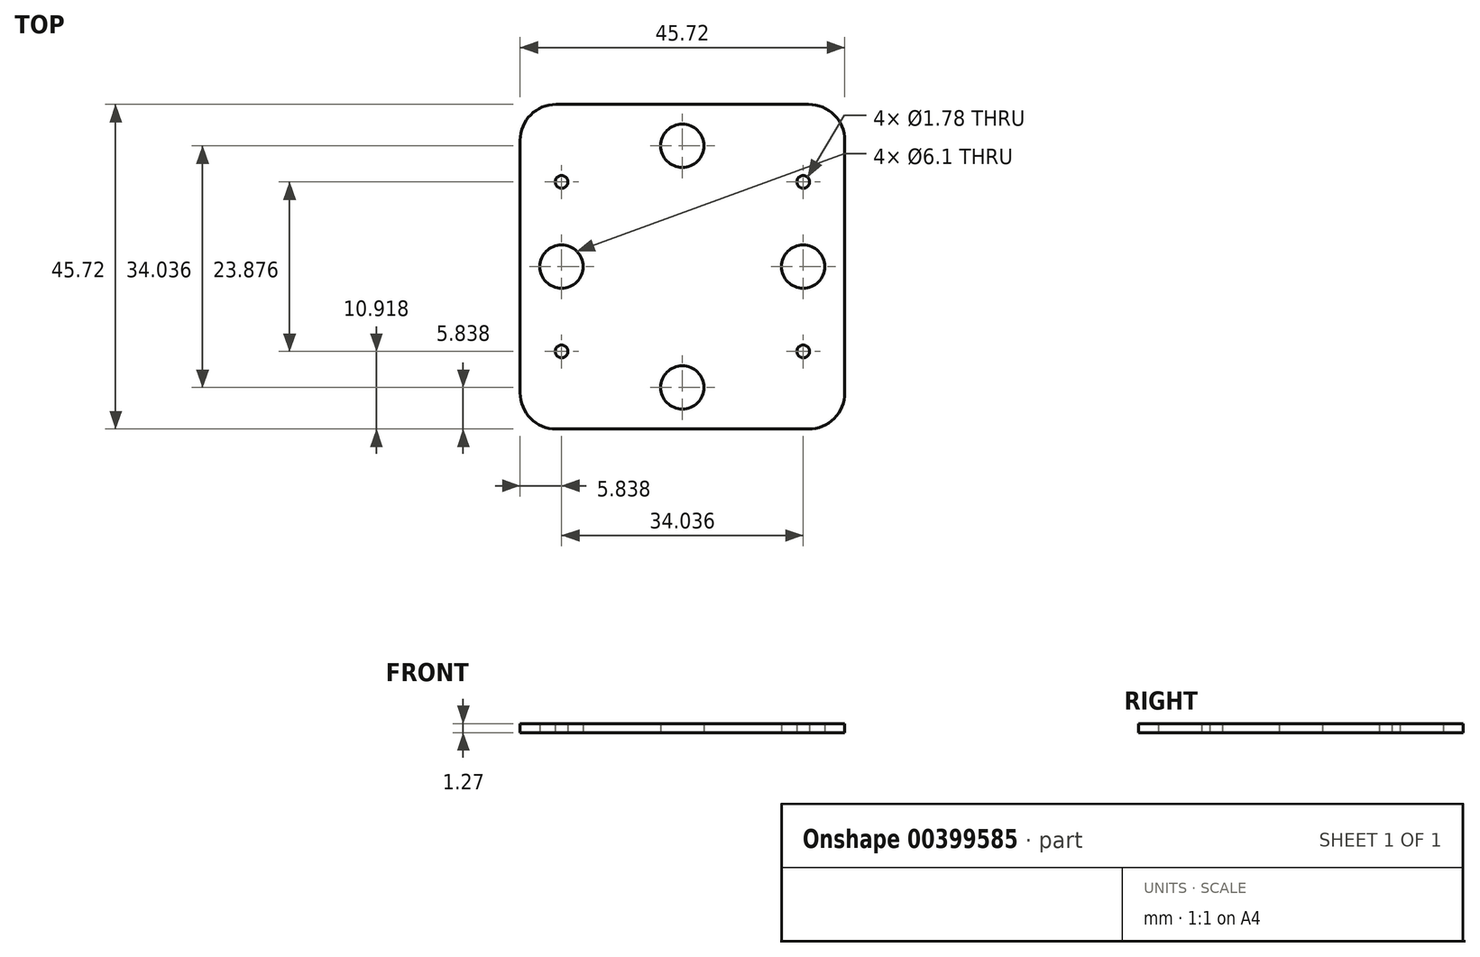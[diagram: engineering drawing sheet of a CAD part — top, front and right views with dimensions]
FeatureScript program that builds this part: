
annotation { "Feature Type Name" : "Feature", "Feature Type Description" : "" }
export const myFeature = defineFeature(function(context is Context, id is Id, definition is map)
    precondition{}
    {
        {
            var Q0;
            Q0=qCreatedBy(makeId("Top.planeOp"),FACE);
            var sketch = newSketch(context, id + "F0", { "sketchPlane" : qUnion([Q0])});
            skLineSegment(sketch, "E0.bottom", {"start": v(-5.96, 25.9) * mm, "end": v(39.76, 25.9) * mm});
            skLineSegment(sketch, "E0.top", {"start": v(-5.96, -19.81) * mm, "end": v(39.76, -19.81) * mm});
            skLineSegment(sketch, "E0.left", {"start": v(-5.96, 25.9) * mm, "end": v(-5.96, -19.81) * mm});
            skLineSegment(sketch, "E0.right", {"start": v(39.76, 25.9) * mm, "end": v(39.76, -19.81) * mm});
            skLineSegment(sketch, "E1.bottom", {"start": v(-0.12, 20.06) * mm, "end": v(33.91, 20.06) * mm});
            skLineSegment(sketch, "E1.top", {"start": v(-0.12, -13.97) * mm, "end": v(33.91, -13.97) * mm});
            skLineSegment(sketch, "E1.left", {"start": v(-0.12, 20.06) * mm, "end": v(-0.12, -13.97) * mm});
            skLineSegment(sketch, "E1.right", {"start": v(33.91, 20.06) * mm, "end": v(33.91, -13.97) * mm});
            skCircle(sketch, "E2", {"center": v(-0.12, 3.05) * mm, "radius": 3.05 * mm});
            skCircle(sketch, "E3", {"center": v(16.9, -13.97) * mm, "radius": 3.05 * mm});
            skCircle(sketch, "E4", {"center": v(33.91, 3.05) * mm, "radius": 3.05 * mm});
            skCircle(sketch, "E5", {"center": v(16.9, 20.06) * mm, "radius": 3.05 * mm});
            skCircle(sketch, "E6", {"center": v(-0.12, 14.98) * mm, "radius": 0.89 * mm});
            skCircle(sketch, "E7", {"center": v(-0.12, -8.9) * mm, "radius": 0.89 * mm});
            skCircle(sketch, "E8", {"center": v(33.91, 14.98) * mm, "radius": 0.89 * mm});
            skCircle(sketch, "E9", {"center": v(33.91, -8.9) * mm, "radius": 0.89 * mm});
            skSolve(sketch);
        }
        {
            var Q0;
            Q0=makeQuery(id+"F0.imprint","IMPRINT",FACE,{"disambiguationData":[TD([[makeQuery(id+"F0.imprint","IMPRINT",EDGE,{"derivedFrom":sQuery(id+"F0.wireOp",EDGE,"E0.bottom")}),-1.0]])]});
            var Q1;
            {var subQ5=sQuery(id+"F0.wireOp",EDGE,"E1.left");var subQ16=sQuery(id+"F0.wireOp",EDGE,"E1.bottom");var subQ17=makeQuery(id+"F0.imprint","INTERSECT",VERTEX,{"derivedFrom":[subQ16,subQ5]});Q1=makeQuery(id+"F0.imprint","IMPRINT",FACE,{"disambiguationData":[TD([[makeQuery(id+"F0.imprint","IMPRINT",EDGE,{"disambiguationData":[TD([[subQ17,-1.0]])],"derivedFrom":subQ16}),-1.0]])]});}
            extrude(context, id + "F1", {"entities" : qUnion([Q0, Q1]), "depth" : 1.27 * mm, "offsetDistance" : 25.4 * mm});
        }
        {
            var Q0;
            Q0=makeQuery(id+"F1.opExtrude","SWEPT_EDGE",EDGE,{"disambiguationData":[OSD([sQuery(id+"F0.wireOp",EDGE,"E0.top"),sQuery(id+"F0.wireOp",EDGE,"E0.left")])]});
            var Q1;
            Q1=makeQuery(id+"F1.opExtrude","SWEPT_EDGE",EDGE,{"disambiguationData":[OSD([sQuery(id+"F0.wireOp",EDGE,"E0.top"),sQuery(id+"F0.wireOp",EDGE,"E0.right")])]});
            var Q2;
            Q2=makeQuery(id+"F1.opExtrude","SWEPT_EDGE",EDGE,{"disambiguationData":[OSD([sQuery(id+"F0.wireOp",EDGE,"E0.bottom"),sQuery(id+"F0.wireOp",EDGE,"E0.right")])]});
            var Q3;
            Q3=makeQuery(id+"F1.opExtrude","SWEPT_EDGE",EDGE,{"disambiguationData":[OSD([sQuery(id+"F0.wireOp",EDGE,"E0.bottom"),sQuery(id+"F0.wireOp",EDGE,"E0.left")])]});
            fillet(context, id + "F2", {"entities" : qUnion([Q0, Q1, Q2, Q3]), "radius" : 5.08 * mm, "tangentPropagation" : true, "allowEdgeOverflow" : false});
        }
    });
